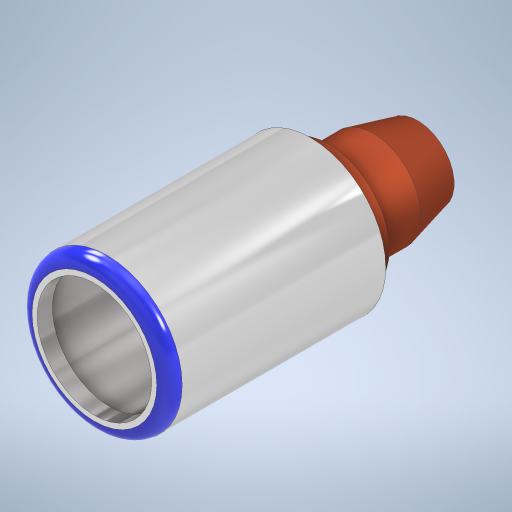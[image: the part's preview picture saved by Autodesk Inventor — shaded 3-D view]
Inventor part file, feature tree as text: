
AUTODESK INVENTOR PART (.ipt)
format: ipt  version: 2023 (Build 270158000, 158)  size: 346,624 bytes
history: native  units: mm
features: sketch x11, extrude x11, other x1, fillet x1
ambient origin geometry x8: Origin, YZ Plane, XZ Plane, XY Plane, X Axis, Y Axis, Z Axis, Center Point
bodies: Body1 (feature_tree)
feature tree (24):
  other  "Твердое тело1"
  sketch  "Эскиз1"
  extrude  "Выдавливание1"  Depth=118.0mm
  extrude  "Выдавливание2"  Depth=150.0mm TaperAngle=0.0deg
  extrude  "Выдавливание3"  Depth=4.0mm
  extrude  "Выдавливание4"  Depth=10.0mm TaperAngle=0.0deg
  sketch  "Эскиз4"
  extrude  "Выдавливание5"  Depth=75.0mm
  extrude  "Выдавливание6"  Depth=35.0mm TaperAngle=0.0deg
  fillet  "Сопряжение1"  Radius=35.0mm
  extrude  "Выдавливание7"  Depth=90.0mm
  extrude  "Выдавливание8"  Depth=20.0mm TaperAngle=0.0deg
  extrude  "Выдавливание9"  Depth=10.0mm
  extrude  "Выдавливание10"  Depth=70.0mm
  extrude  "Выдавливание11"  Depth=55.0mm
  sketch  "Эскиз2"
  sketch  "Эскиз3"
  sketch  "Эскиз5"
  sketch  "Эскиз6"
  sketch  "Эскиз7"
  sketch  "Эскиз8"
  sketch  "Эскиз9"
  sketch  "Эскиз10"
  sketch  "Эскиз11"
